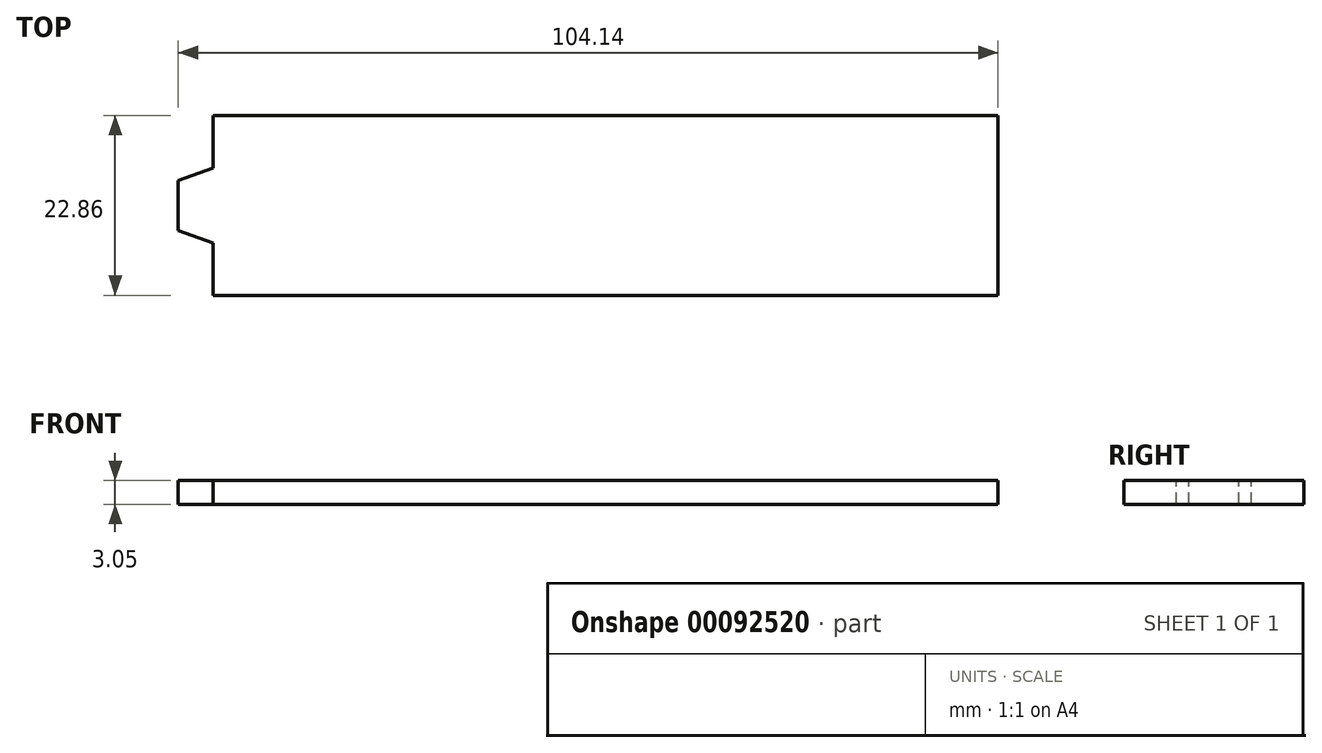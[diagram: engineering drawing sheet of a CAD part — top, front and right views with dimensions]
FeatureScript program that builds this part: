
annotation { "Feature Type Name" : "Feature", "Feature Type Description" : "" }
export const myFeature = defineFeature(function(context is Context, id is Id, definition is map)
    precondition{}
    {
        {
            var Q0;
            Q0=qCreatedBy(makeId("Top.planeOp"),FACE);
            var sketch = newSketch(context, id + "F0", { "sketchPlane" : qUnion([Q0])});
            skLineSegment(sketch, "E0.bottom", {"start": v(0, 0) * mm, "end": v(-99.7, 0) * mm});
            skLineSegment(sketch, "E0.top", {"start": v(0, 22.86) * mm, "end": v(-99.7, 22.86) * mm});
            skLineSegment(sketch, "E0.left", {"start": v(0, 0) * mm, "end": v(0, 22.86) * mm});
            skLineSegment(sketch, "E0.right", {"start": v(-99.7, 0) * mm, "end": v(-99.7, 22.86) * mm});
            skLineSegment(sketch, "E1", {"start": v(-99.7, 11.43) * mm, "end": v(0, 11.43) * mm, "construction": true});
            skLineSegment(sketch, "E2", {"start": v(-99.7, 11.43) * mm, "end": v(-104.14, 11.43) * mm});
            skLineSegment(sketch, "E3", {"start": v(-104.14, 11.43) * mm, "end": v(-104.14, 14.6) * mm});
            skLineSegment(sketch, "E4", {"start": v(-104.14, 14.6) * mm, "end": v(-99.7, 16.2) * mm});
            skLineSegment(sketch, "E5.MirrorCS", {"start": v(-104.14, 8.25) * mm, "end": v(-99.7, 6.67) * mm});
            skLineSegment(sketch, "E6.MirrorCS", {"start": v(-104.14, 11.43) * mm, "end": v(-104.14, 8.25) * mm});
            skSolve(sketch);
        }
        {
            var Q0;
            Q0 = qSketchRegion(id + "F0", true);
            extrude(context, id + "F1", {"entities" : qUnion([Q0]), "oppositeDirection" : true, "depth" : 3.05 * mm});
        }
    });
